# Revit family: Faucet-Flush_Actuator_Sensor-KOHLER-Beam-K-30941T
name_source: partatom
category: Plumbing Fixtures
units: mm (PartAtom-declared; Revit-internal decimal feet)

## family parameters
Cut with Voids When Loaded = No
Host = Face
Maintain Annotation Orientation = No
OmniClass Number = 23.31.11.00
OmniClass Title = Faucets
Part Type = Normal
Room Calculation Point = No
Round Connector Dimension = Use Diameter
Shared = No

## types (6) — shared parameters
ADA Compliant = No
Apparent Load = 0 VA
Assembly Code = D2010
CW Connection = Yes
Cold Water Inlet = Cold Water Inlet
Cold Water Outlet = Cold Water Outlet
Date Modified = 09/28/2023
Default Elevation = 36"
Drain Included = No
Electrical Connector = Yes
Electrical Note = One Dedicated Circuit Required
Flow Rate = 0 GPM
HW Connection = No
Height = 4 15/16"
Hot Water Inlet = Hot Water Inlet
Length = 3 1/2"
Manufacturer = Kohler Co.
Master Format 2014 = 22 41 39
Master Format 2014 Name = Residential Faucets, Supplies, and Trim
Material = Premium Metal Construction
Pressure = 80.00 psi
Product Name = Beam
URL = http://www.kohler.com.cn
Vent Connection = No
Voltage = 200 V
Waste Connection = No
Waste Water Outlet = Waste Water Outlet
WaterSense Certified = No
Width = 4 15/16"

## per-type parameters (varying)
| type | Description | Finish | Flush Rate 2.5 LPF | Model | Product Documentation Link | Product Page URL | Type |
| CP-Polished Chrome | Super Water Saving Urinal Sensor, AC Type | Kohler-Metal-CP-Polished_Chrome | No | K-30941T-CP | https://files.kohler.com.cn | https://www.kohler.com.cn | 1 |
| BN-Vibrant Brushed Nickel | Super Water Saving Urinal Sensor, AC Type | Kohler-Metal-BN-Vibrant_Brushed_Nickel | No | K-30941T-BN | https://files.kohler.com.cn | https://www.kohler.com.cn | 2 |
| 2W, CP-Polished Chrome | Eco Urinal Sensor 0.5/1 LPF | Kohler-Metal-CP-Polished_Chrome | No | K-30941T-2W-CP |  |  | 3 |
| 2W, BN-Vibrant Brushed Nickel | Eco Urinal Sensor 0.5/1 LPF | Kohler-Metal-BN-Vibrant_Brushed_Nickel | No | K-30941T-2W-BN |  |  | 4 |
| 2, CP-Polished Chrome | Eco Urinal Sensor 2.5 LPF | Kohler-Metal-CP-Polished_Chrome | Yes | K-30941T-2-CP |  |  | 5 |
| 2, BN-Vibrant Brushed Nickel | Eco Urinal Sensor 2.5 LPF | Kohler-Metal-BN-Vibrant_Brushed_Nickel | Yes | K-30941T-2-BN |  |  | 6 |

## geometry (parser evidence)
native form markers: Sweep x6
no freeform markers — native parametric forms only
